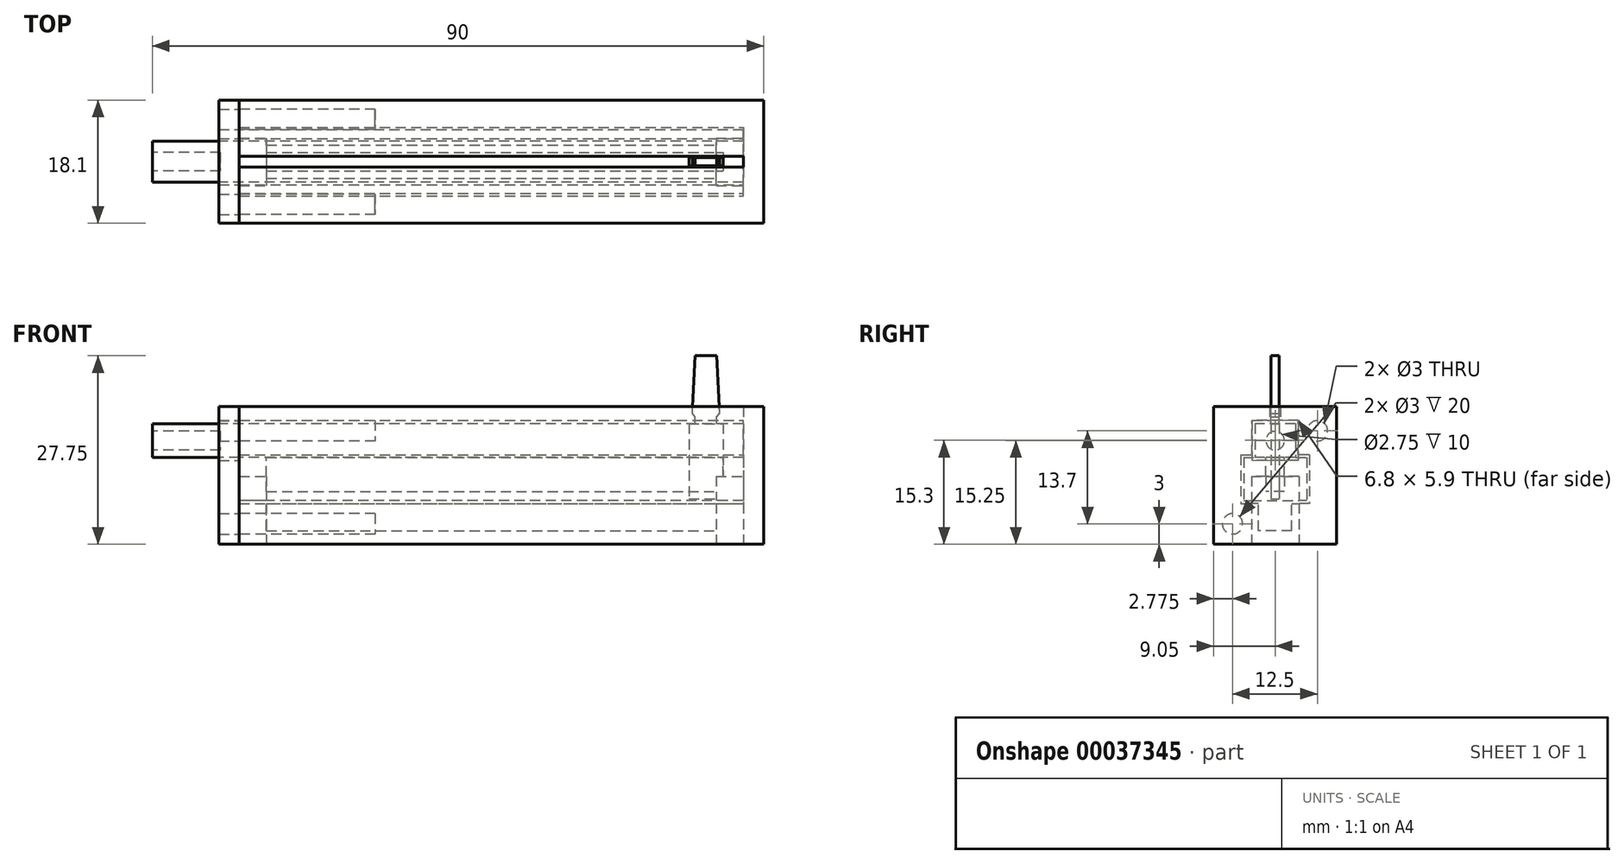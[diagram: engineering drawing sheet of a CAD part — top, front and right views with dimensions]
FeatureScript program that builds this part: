
annotation { "Feature Type Name" : "Feature", "Feature Type Description" : "" }
export const myFeature = defineFeature(function(context is Context, id is Id, definition is map)
    precondition{}
    {
        {
            var Q0;
            Q0=qCreatedBy(makeId("Top.planeOp"),FACE);
            var sketch = newSketch(context, id + "F0", { "sketchPlane" : qUnion([Q0])});
            skLineSegment(sketch, "E0", {"start": v(-37.74, 0) * mm, "end": v(-37.74, -9.3) * mm});
            skLineSegment(sketch, "E1", {"start": v(-37.74, -9.3) * mm, "end": v(36.46, -9.3) * mm});
            skLineSegment(sketch, "E2", {"start": v(36.46, -9.3) * mm, "end": v(36.46, 0) * mm});
            skLineSegment(sketch, "E3", {"start": v(36.46, 0) * mm, "end": v(-37.74, 0) * mm});
            skSolve(sketch);
        }
        {
            var Q0;
            Q0=makeQuery(id+"F0.imprint","IMPRINT",FACE,{"disambiguationData":[TD([[makeQuery(id+"F0.imprint","IMPRINT",EDGE,{"derivedFrom":sQuery(id+"F0.wireOp",EDGE,"E0")}),1.0]])]});
            extrude(context, id + "F1", {"entities" : qUnion([Q0]), "depth" : 6.35 * mm});
        }
        {
            var Q0;
            Q0=makeQuery(id+"F1.opExtrude","CAP_FACE",FACE,{"disambiguationData":[OSD([sQuery(id+"F0.wireOp",EDGE,"E0"),sQuery(id+"F0.wireOp",EDGE,"E1"),sQuery(id+"F0.wireOp",EDGE,"E2"),sQuery(id+"F0.wireOp",EDGE,"E3")])],"isStart":false});
            var sketch = newSketch(context, id + "F2", { "sketchPlane" : qUnion([Q0])});
            skLineSegment(sketch, "E4.bottom", {"start": v(-33.74, -3.3) * mm, "end": v(33.46, -3.3) * mm});
            skLineSegment(sketch, "E4.top", {"start": v(-33.74, -6) * mm, "end": v(33.46, -6) * mm});
            skLineSegment(sketch, "E4.left", {"start": v(-33.74, -3.3) * mm, "end": v(-33.74, -6) * mm});
            skLineSegment(sketch, "E4.right", {"start": v(33.46, -3.3) * mm, "end": v(33.46, -6) * mm});
            skSolve(sketch);
        }
        {
            var Q0;
            Q0=makeQuery(id+"F2.imprint","IMPRINT",FACE,{"disambiguationData":[TD([[makeQuery(id+"F2.imprint","IMPRINT",EDGE,{"derivedFrom":sQuery(id+"F2.wireOp",EDGE,"E4.bottom")}),-1.0]])]});
            extrude(context, id + "F3", {"entities" : qUnion([Q0]), "operationType" : NewBodyOperationType.REMOVE, "oppositeDirection" : true, "depth" : 5 * mm});
        }
        {
            var Q0;
            Q0=qCreatedBy(makeId("Right.planeOp"),FACE);
            var sketch = newSketch(context, id + "F4", { "sketchPlane" : qUnion([Q0])});
            skPoint(sketch, "E5", {"position": v(-4.65, 0) * mm});
            skLineSegment(sketch, "E6", {"start": v(-4.65, 0) * mm, "end": v(0, 0) * mm});
            skSolve(sketch);
        }
        {
            var Q0;
            Q0=makeQuery(id+"F1.opExtrude","SWEPT_BODY",BODY,{"disambiguationData":[OSD([sQuery(id+"F0.wireOp",EDGE,"E0"),sQuery(id+"F0.wireOp",EDGE,"E1"),sQuery(id+"F0.wireOp",EDGE,"E2"),sQuery(id+"F0.wireOp",EDGE,"E3")])]});
            transform(context, id + "F5", {"entities" : qUnion([Q0]), "transformType" : TransformType.TRANSLATION_3D, "dx" : 0 * mm, "dy" : 4.65 * mm, "dz" : 0 * mm, "makeCopy" : false});
        }
        {
            var Q0;
            Q0=qCreatedBy(makeId("Front.planeOp"),FACE);
            var sketch = newSketch(context, id + "F6", { "sketchPlane" : qUnion([Q0])});
            skLineSegment(sketch, "E7.bottom", {"start": v(28.46, 0.29) * mm, "end": v(33.46, 0.29) * mm});
            skLineSegment(sketch, "E8", {"start": v(33.46, 11.35) * mm, "end": v(32.54, 11.35) * mm});
            skLineSegment(sketch, "E9", {"start": v(32.96, 12.85) * mm, "end": v(32.56, 21.35) * mm});
            skLineSegment(sketch, "E10", {"start": v(32.54, 11.35) * mm, "end": v(32.54, 12.32) * mm});
            skLineSegment(sketch, "E11", {"start": v(32.54, 12.32) * mm, "end": v(32.96, 12.85) * mm});
            skLineSegment(sketch, "E12", {"start": v(30.96, 21.35) * mm, "end": v(32.56, 21.35) * mm});
            skLineSegment(sketch, "E13.0.MirrorCS", {"start": v(30.96, 21.35) * mm, "end": v(29.36, 21.35) * mm});
            skLineSegment(sketch, "E14.0.MirrorCS", {"start": v(28.96, 12.85) * mm, "end": v(29.36, 21.35) * mm});
            skLineSegment(sketch, "E15.0.MirrorCS", {"start": v(29.39, 12.32) * mm, "end": v(28.96, 12.85) * mm});
            skLineSegment(sketch, "E16.0.MirrorCS", {"start": v(29.39, 11.35) * mm, "end": v(29.39, 12.32) * mm});
            skLineSegment(sketch, "E17.0.MirrorCS", {"start": v(28.46, 11.35) * mm, "end": v(29.39, 11.35) * mm});
            skLineSegment(sketch, "E18", {"start": v(33.46, 11.35) * mm, "end": v(33.46, 0.29) * mm});
            skLineSegment(sketch, "E19", {"start": v(28.46, 11.35) * mm, "end": v(28.46, 0.29) * mm});
            skSolve(sketch);
        }
        {
            var Q0;
            Q0=qSketchRegion(id+"F6",true);
            extrude(context, id + "F7", {"entities" : qUnion([Q0]), "endBound" : BoundingType.SYMMETRIC, "depth" : 1.2 * mm});
        }
        {
            var Q0;
            Q0=makeQuery(id+"F1.opExtrude","CAP_FACE",FACE,{"disambiguationData":[OSD([sQuery(id+"F0.wireOp",EDGE,"E0"),sQuery(id+"F0.wireOp",EDGE,"E1"),sQuery(id+"F0.wireOp",EDGE,"E2"),sQuery(id+"F0.wireOp",EDGE,"E3")])],"isStart":false});
            cPlane(context, id + "F8", {"entities" : qUnion([Q0]), "cplaneType" : CPlaneType.OFFSET, "offset" : 0 * mm, "width" : 150 * mm, "height" : 150 * mm});
        }
        {
            var Q0;
            Q0=qCreatedBy(id+"F8.planeOp",FACE);
            var sketch = newSketch(context, id + "F9", { "sketchPlane" : qUnion([Q0])});
            skLineSegment(sketch, "E20.bottom", {"start": v(36.46, 3) * mm, "end": v(-50.54, 3) * mm});
            skLineSegment(sketch, "E20.top", {"start": v(36.46, -3) * mm, "end": v(-50.54, -3) * mm});
            skLineSegment(sketch, "E20.left", {"start": v(36.46, 3) * mm, "end": v(36.46, -3) * mm});
            skLineSegment(sketch, "E20.right", {"start": v(-50.54, 3) * mm, "end": v(-50.54, -3) * mm});
            skPoint(sketch, "E21", {"position": v(36.46, 0) * mm});
            skLineSegment(sketch, "E22.bottom", {"start": v(28.46, -0.6) * mm, "end": v(33.46, -0.6) * mm});
            skLineSegment(sketch, "E22.top", {"start": v(28.46, 0.6) * mm, "end": v(33.46, 0.6) * mm});
            skLineSegment(sketch, "E22.left", {"start": v(28.46, -0.6) * mm, "end": v(28.46, 0.6) * mm});
            skLineSegment(sketch, "E22.right", {"start": v(33.46, -0.6) * mm, "end": v(33.46, 0.6) * mm});
            skSolve(sketch);
        }
        {
            var Q0;
            Q0=makeQuery(id+"F9.imprint","IMPRINT",FACE,{"disambiguationData":[TD([[makeQuery(id+"F9.imprint","IMPRINT",EDGE,{"derivedFrom":sQuery(id+"F9.wireOp",EDGE,"E20.bottom")}),1.0]])]});
            extrude(context, id + "F10", {"entities" : qUnion([Q0]), "depth" : 5 * mm});
        }
        {
            var Q0;
            Q0=makeQuery(id+"F1.opExtrude","SWEPT_FACE",FACE,{"disambiguationData":[OSD([sQuery(id+"F0.wireOp",EDGE,"E2")])]});
            cPlane(context, id + "F11", {"entities" : qUnion([Q0]), "cplaneType" : CPlaneType.OFFSET, "offset" : 0 * mm, "width" : 150 * mm, "height" : 150 * mm});
        }
        {
            var Q0;
            Q0=qCreatedBy(id+"F11.planeOp",FACE);
            var sketch = newSketch(context, id + "F12", { "sketchPlane" : qUnion([Q0])});
            skLineSegment(sketch, "E23.left", {"start": v(-9.05, -6.4) * mm, "end": v(-9.05, 13.85) * mm});
            skLineSegment(sketch, "E24", {"start": v(-9.05, 13.85) * mm, "end": v(-0.8, 13.85) * mm});
            skLineSegment(sketch, "E25", {"start": v(-0.8, 13.85) * mm, "end": v(-0.8, 11.85) * mm});
            skLineSegment(sketch, "E26", {"start": v(-9.05, -6.4) * mm, "end": v(0, -6.4) * mm});
            skLineSegment(sketch, "E27", {"start": v(-5.05, 6.75) * mm, "end": v(-3.4, 6.75) * mm});
            skLineSegment(sketch, "E28", {"start": v(-3.4, 6.75) * mm, "end": v(-3.4, 11.85) * mm});
            skLineSegment(sketch, "E29", {"start": v(-3.4, 11.85) * mm, "end": v(-0.8, 11.85) * mm});
            skLineSegment(sketch, "E30", {"start": v(-5.05, 6.75) * mm, "end": v(-5.05, -0.4) * mm});
            skPoint(sketch, "E31", {"position": v(-4.65, 0) * mm});
            skLineSegment(sketch, "E32", {"start": v(-2.45, -0.4) * mm, "end": v(-2.45, -4.4) * mm});
            skLineSegment(sketch, "E33", {"start": v(-2.45, -4.4) * mm, "end": v(0, -4.4) * mm});
            skLineSegment(sketch, "E34", {"start": v(-5.05, -0.4) * mm, "end": v(-2.45, -0.4) * mm});
            skLineSegment(sketch, "E35", {"start": v(0, -4.4) * mm, "end": v(0, -6.4) * mm});
            skPoint(sketch, "E36.0.MirrorP", {"position": v(4.65, 0) * mm});
            skLineSegment(sketch, "E36.1.MirrorCS", {"start": v(9.05, -6.4) * mm, "end": v(9.05, 13.85) * mm});
            skLineSegment(sketch, "E36.2.MirrorCS", {"start": v(5.05, 6.75) * mm, "end": v(3.4, 6.75) * mm});
            skLineSegment(sketch, "E36.3.MirrorCS", {"start": v(2.45, -0.4) * mm, "end": v(2.45, -4.4) * mm});
            skLineSegment(sketch, "E36.4.MirrorCS", {"start": v(5.05, 6.75) * mm, "end": v(5.05, -0.4) * mm});
            skLineSegment(sketch, "E36.5.MirrorCS", {"start": v(3.4, 11.85) * mm, "end": v(0.8, 11.85) * mm});
            skLineSegment(sketch, "E36.6.MirrorCS", {"start": v(0.8, 13.85) * mm, "end": v(0.8, 11.85) * mm});
            skLineSegment(sketch, "E36.7.MirrorCS", {"start": v(9.05, 13.85) * mm, "end": v(0.8, 13.85) * mm});
            skLineSegment(sketch, "E36.8.MirrorCS", {"start": v(9.05, -6.4) * mm, "end": v(0, -6.4) * mm});
            skLineSegment(sketch, "E36.9.MirrorCS", {"start": v(2.45, -4.4) * mm, "end": v(0, -4.4) * mm});
            skLineSegment(sketch, "E36.10.MirrorCS", {"start": v(3.4, 6.75) * mm, "end": v(3.4, 11.85) * mm});
            skLineSegment(sketch, "E36.11.MirrorCS", {"start": v(5.05, -0.4) * mm, "end": v(2.45, -0.4) * mm});
            skSolve(sketch);
        }
        {
            var Q0;
            Q0=qSketchRegion(id+"F12",true);
            extrude(context, id + "F13", {"entities" : qUnion([Q0]), "oppositeDirection" : true, "depth" : 74.2 * mm});
        }
        {
            var Q0;
            Q0=qCreatedBy(id+"F11.planeOp",FACE);
            var sketch = newSketch(context, id + "F14", { "sketchPlane" : qUnion([Q0])});
            skLineSegment(sketch, "E37.bottom", {"start": v(-9.05, 13.85) * mm, "end": v(9.05, 13.85) * mm});
            skLineSegment(sketch, "E37.top", {"start": v(-9.05, -6.4) * mm, "end": v(9.05, -6.4) * mm});
            skLineSegment(sketch, "E37.left", {"start": v(-9.05, 13.85) * mm, "end": v(-9.05, -6.4) * mm});
            skLineSegment(sketch, "E37.right", {"start": v(9.05, 13.85) * mm, "end": v(9.05, -6.4) * mm});
            skSolve(sketch);
        }
        {
            var Q0;
            Q0=qSketchRegion(id+"F14",true);
            extrude(context, id + "F15", {"entities" : qUnion([Q0]), "operationType" : NewBodyOperationType.ADD, "depth" : 3 * mm});
        }
        {
            var Q0;
            Q0=makeQuery(id+"F13.opExtrude","CAP_FACE",FACE,{"disambiguationData":[OSD([sQuery(id+"F12.wireOp",EDGE,"E23.left"),sQuery(id+"F12.wireOp",EDGE,"E24"),sQuery(id+"F12.wireOp",EDGE,"E25"),sQuery(id+"F12.wireOp",EDGE,"E26"),sQuery(id+"F12.wireOp",EDGE,"E27"),sQuery(id+"F12.wireOp",EDGE,"E28"),sQuery(id+"F12.wireOp",EDGE,"E29"),sQuery(id+"F12.wireOp",EDGE,"E30"),sQuery(id+"F12.wireOp",EDGE,"E32"),sQuery(id+"F12.wireOp",EDGE,"E33"),sQuery(id+"F12.wireOp",EDGE,"E34"),sQuery(id+"F12.wireOp",EDGE,"E36.1.MirrorCS"),sQuery(id+"F12.wireOp",EDGE,"E36.2.MirrorCS"),sQuery(id+"F12.wireOp",EDGE,"E36.3.MirrorCS"),sQuery(id+"F12.wireOp",EDGE,"E36.4.MirrorCS"),sQuery(id+"F12.wireOp",EDGE,"E36.5.MirrorCS"),sQuery(id+"F12.wireOp",EDGE,"E36.6.MirrorCS"),sQuery(id+"F12.wireOp",EDGE,"E36.7.MirrorCS"),sQuery(id+"F12.wireOp",EDGE,"E36.8.MirrorCS"),sQuery(id+"F12.wireOp",EDGE,"E36.9.MirrorCS"),sQuery(id+"F12.wireOp",EDGE,"E36.10.MirrorCS"),sQuery(id+"F12.wireOp",EDGE,"E36.11.MirrorCS")])],"isStart":false});
            cPlane(context, id + "F16", {"entities" : qUnion([Q0]), "cplaneType" : CPlaneType.OFFSET, "offset" : 0 * mm, "width" : 150 * mm, "height" : 150 * mm});
        }
        {
            var Q0;
            Q0=qCreatedBy(id+"F16.planeOp",FACE);
            var sketch = newSketch(context, id + "F17", { "sketchPlane" : qUnion([Q0])});
            skLineSegment(sketch, "E38.bottom", {"start": v(-9.05, 13.85) * mm, "end": v(9.05, 13.85) * mm});
            skLineSegment(sketch, "E38.top", {"start": v(-9.05, -6.4) * mm, "end": v(9.05, -6.4) * mm});
            skLineSegment(sketch, "E38.left", {"start": v(-9.05, 13.85) * mm, "end": v(-9.05, -6.4) * mm});
            skLineSegment(sketch, "E38.right", {"start": v(9.05, 13.85) * mm, "end": v(9.05, -6.4) * mm});
            skLineSegment(sketch, "E39.bottom", {"start": v(-3.4, 11.85) * mm, "end": v(3.4, 11.85) * mm});
            skLineSegment(sketch, "E39.top", {"start": v(-3.4, 5.95) * mm, "end": v(3.4, 5.95) * mm});
            skLineSegment(sketch, "E39.left", {"start": v(-3.4, 11.85) * mm, "end": v(-3.4, 5.95) * mm});
            skLineSegment(sketch, "E39.right", {"start": v(3.4, 11.85) * mm, "end": v(3.4, 5.95) * mm});
            skLineSegment(sketch, "E40", {"start": v(-3.4, 5.95) * mm, "end": v(-3.4, 6.75) * mm});
            skLineSegment(sketch, "E41", {"start": v(-3.4, 6.75) * mm, "end": v(-3.4, 6.35) * mm});
            skSolve(sketch);
        }
        {
            var Q0;
            Q0=makeQuery(id+"F15.boolean.opBoolean","MERGE",FACE,{"derivedFrom":[makeQuery(id+"F13.opExtrude","SWEPT_FACE",FACE,{"disambiguationData":[OSD([sQuery(id+"F12.wireOp",EDGE,"E26"),sQuery(id+"F12.wireOp",EDGE,"E36.8.MirrorCS")])]}),makeQuery(id+"F15.opExtrude","SWEPT_FACE",FACE,{"disambiguationData":[OSD([sQuery(id+"F14.wireOp",EDGE,"E37.top")])]})]});
            var sketch = newSketch(context, id + "F18", { "sketchPlane" : qUnion([Q0])});
            skLineSegment(sketch, "E42.bottom", {"start": v(-37.74, -3.5) * mm, "end": v(-33.74, -3.5) * mm});
            skLineSegment(sketch, "E42.top", {"start": v(-37.74, 3.5) * mm, "end": v(-33.74, 3.5) * mm});
            skLineSegment(sketch, "E42.left", {"start": v(-37.74, -3.5) * mm, "end": v(-37.74, 3.5) * mm});
            skLineSegment(sketch, "E42.right", {"start": v(-33.74, -3.5) * mm, "end": v(-33.74, 3.5) * mm});
            skLineSegment(sketch, "E43.bottom", {"start": v(32.46, 3.5) * mm, "end": v(36.46, 3.5) * mm});
            skLineSegment(sketch, "E43.top", {"start": v(32.46, -3.5) * mm, "end": v(36.46, -3.5) * mm});
            skLineSegment(sketch, "E43.left", {"start": v(32.46, 3.5) * mm, "end": v(32.46, -3.5) * mm});
            skLineSegment(sketch, "E43.right", {"start": v(36.46, 3.5) * mm, "end": v(36.46, -3.5) * mm});
            skPoint(sketch, "E44", {"position": v(-37.74, 0) * mm});
            skPoint(sketch, "E45", {"position": v(36.46, 0) * mm});
            skSolve(sketch);
        }
        {
            var Q0;
            Q0=qSketchRegion(id+"F18",true);
            extrude(context, id + "F19", {"entities" : qUnion([Q0]), "operationType" : NewBodyOperationType.REMOVE, "oppositeDirection" : true, "depth" : 10 * mm});
        }
        {
            var Q0;
            Q0=makeQuery(id+"F10.opExtrude","SWEPT_FACE",FACE,{"disambiguationData":[OSD([sQuery(id+"F9.wireOp",EDGE,"E20.right")])]});
            var sketch = newSketch(context, id + "F20", { "sketchPlane" : qUnion([Q0])});
            skLineSegment(sketch, "E46", {"start": v(0, 11.35) * mm, "end": v(0, 6.35) * mm});
            skCircle(sketch, "E47", {"center": v(0, 8.85) * mm, "radius": 1.38 * mm});
            skPoint(sketch, "E48", {"position": v(0, 10.23) * mm});
            skPoint(sketch, "E49", {"position": v(0, 7.47) * mm});
            skCircle(sketch, "E50", {"center": v(0, 8.85) * mm, "radius": 3.9 * mm});
            skSolve(sketch);
        }
        {
            var Q0;
            {var subQ0=sQuery(id+"F20.wireOp",EDGE,"E47");var subQ1=sQuery(id+"F20.wireOp",EDGE,"E46");var subQ3=makeQuery(id+"F20.imprint","INTERSECT",VERTEX,{"disambiguationData":[OD(0.0)],"derivedFrom":[subQ1,subQ0]});Q0=makeQuery(id+"F20.imprint","IMPRINT",FACE,{"disambiguationData":[TD([[makeQuery(id+"F20.imprint","IMPRINT",EDGE,{"disambiguationData":[TD([[subQ3,-1.0]])],"derivedFrom":subQ1}),1.0]])]});}
            var Q1;
            {var subQ0=sQuery(id+"F20.wireOp",EDGE,"E47");var subQ1=sQuery(id+"F20.wireOp",EDGE,"E46");var subQ3=makeQuery(id+"F20.imprint","INTERSECT",VERTEX,{"disambiguationData":[OD(0.0)],"derivedFrom":[subQ1,subQ0]});Q1=makeQuery(id+"F20.imprint","IMPRINT",FACE,{"disambiguationData":[TD([[makeQuery(id+"F20.imprint","IMPRINT",EDGE,{"disambiguationData":[TD([[subQ3,-1.0]])],"derivedFrom":subQ1}),-1.0]])]});}
            var Q2;
            {var subQ0=sQuery(id+"F20.wireOp",EDGE,"E50");var subQ1=makeQuery(id+"FxfemGlf4V9sQEC_4.opExtrude","CAP_FACE",FACE,{"disambiguationData":[OSD([sQuery(id+"F20.wireOp",EDGE,"E47"),subQ0])],"isStart":false});var subQ2=sQuery(id+"F9.wireOp",EDGE,"E20.top");var subQ3=sQuery(id+"F9.wireOp",EDGE,"E20.bottom");Q2=makeQuery(id+"FxfemGlf4V9sQEC_4.boolean.opBoolean","SPLIT",FACE,{"disambiguationData":[TD([makeQuery(id+"F10.opExtrude","SWEPT_FACE",FACE,{"disambiguationData":[OSD([subQ3])]}),makeQuery(id+"F10.opExtrude","CAP_FACE",FACE,{"disambiguationData":[OSD([subQ3,subQ2,sQuery(id+"F9.wireOp",EDGE,"E20.left"),sQuery(id+"F9.wireOp",EDGE,"E20.right"),sQuery(id+"F9.wireOp",EDGE,"E22.bottom"),sQuery(id+"F9.wireOp",EDGE,"E22.top"),sQuery(id+"F9.wireOp",EDGE,"E22.left"),sQuery(id+"F9.wireOp",EDGE,"E22.right")])],"isStart":false}),makeQuery(id+"F10.opExtrude","SWEPT_FACE",FACE,{"disambiguationData":[OSD([subQ2])]}),subQ1,makeQuery(id+"FxfemGlf4V9sQEC_4.opExtrude","SWEPT_FACE",FACE,{"disambiguationData":[OSD([subQ0])]})])],"derivedFrom":subQ1});}
            extrude(context, id + "F21", {"entities" : qUnion([Q0, Q1]), "operationType" : NewBodyOperationType.REMOVE, "oppositeDirection" : true, "endBoundEntityFace" : qUnion([Q2]), "depth" : 10 * mm});
        }
        {
            var Q0;
            Q0=makeQuery(id+"F17.imprint","IMPRINT",FACE,{"disambiguationData":[TD([[makeQuery(id+"F17.imprint","IMPRINT",EDGE,{"derivedFrom":sQuery(id+"F17.wireOp",EDGE,"E38.bottom")}),-1.0]])]});
            var sketch = newSketch(context, id + "F22", { "sketchPlane" : qUnion([Q0])});
            skCircle(sketch, "E51", {"center": v(-6.23, 10.3) * mm, "radius": 1.5 * mm});
            skLineSegment(sketch, "E52", {"start": v(-6.23, 8.8) * mm, "end": v(-6.23, 11.8) * mm});
            skLineSegment(sketch, "E53", {"start": v(-6.23, 6.75) * mm, "end": v(-6.23, 13.85) * mm});
            skLineSegment(sketch, "E54", {"start": v(-3.4, 10.3) * mm, "end": v(-9.05, 10.3) * mm});
            skCircle(sketch, "E55", {"center": v(6.27, -3.4) * mm, "radius": 1.5 * mm});
            skLineSegment(sketch, "E56", {"start": v(6.27, -4.9) * mm, "end": v(6.27, -1.9) * mm});
            skLineSegment(sketch, "E57", {"start": v(3.5, -3.4) * mm, "end": v(9.05, -3.4) * mm});
            skSolve(sketch);
        }
        {
            var Q0;
            Q0=qSketchRegion(id+"F22",true);
            extrude(context, id + "F23", {"entities" : qUnion([Q0]), "operationType" : NewBodyOperationType.REMOVE, "oppositeDirection" : true, "depth" : 20 * mm});
        }
        {
            var Q0;
            Q0=qSketchRegion(id+"F17",true);
            extrude(context, id + "F24", {"entities" : qUnion([Q0]), "depth" : 3 * mm});
        }
        {
            var Q0;
            Q0=qSketchRegion(id+"F22",true);
            var Q1;
            Q1=makeQuery(id+"F24.opExtrude","CAP_FACE",FACE,{"disambiguationData":[OSD([sQuery(id+"F17.wireOp",EDGE,"E38.bottom"),sQuery(id+"F17.wireOp",EDGE,"E38.top"),sQuery(id+"F17.wireOp",EDGE,"E38.left"),sQuery(id+"F17.wireOp",EDGE,"E38.right"),sQuery(id+"F17.wireOp",EDGE,"E39.bottom"),sQuery(id+"F17.wireOp",EDGE,"E39.top"),sQuery(id+"F17.wireOp",EDGE,"E39.left"),sQuery(id+"F17.wireOp",EDGE,"E39.right"),sQuery(id+"F17.wireOp",EDGE,"E40"),sQuery(id+"F17.wireOp",EDGE,"E41")])],"isStart":false});
            extrude(context, id + "F25", {"entities" : qUnion([Q0]), "operationType" : NewBodyOperationType.REMOVE, "endBound" : BoundingType.UP_TO_SURFACE, "endBoundEntityFace" : qUnion([Q1]), "depth" : 25 * mm});
        }
    });
